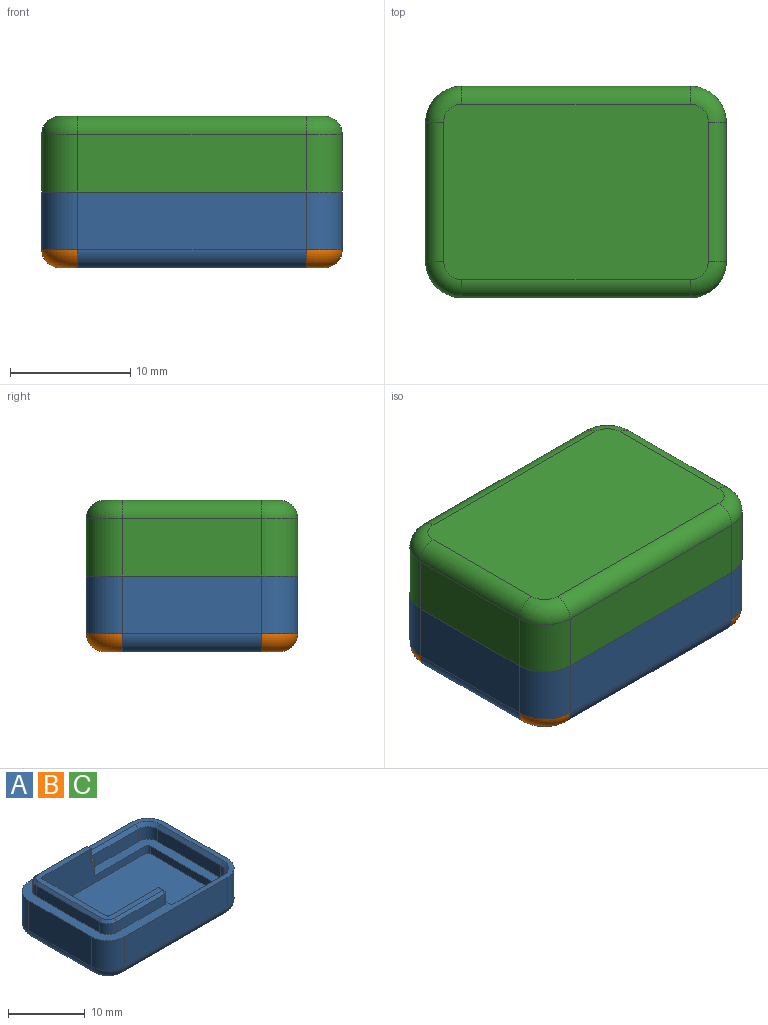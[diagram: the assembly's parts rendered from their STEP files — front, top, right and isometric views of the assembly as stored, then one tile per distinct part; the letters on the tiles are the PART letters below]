
ASSEMBLY  parts=3 mates=1
PART A: 61 faces, bbox 25.5x18.1x8.4 mm
  f0: plane 25x17.6mm, normal (0,0,1), area 80.8mm2, adj f3,f4,f6,f7,f8,f9,f10,f11
  f1: plane 11.6x1.2mm, normal (-1,0,0), area 13.9mm2, adj f2,f5,f18,f34
  f2: cylinder r=0.4mm len=1.2mm, axis (0,0,-1), area 0.8mm2, adj f1,f3,f18,f34
  f3: plane 19x5.8mm, normal (0,-1,0), area 65.1mm2, adj f0,f2,f15,f18,f28,f34,f35,f46
  f4: plane 19x5.8mm, normal (0,1,0), area 65.1mm2, adj f0,f5,f17,f18,f29,f34,f45,f46
  f5: cylinder r=0.4mm len=1.2mm, axis (0,0,-1), area 0.8mm2, adj f1,f4,f18,f34
  f6: plane 11.6x4.8mm, normal (1,0,0), area 55.7mm2, adj f0,f7,f13,f22
  f7: cylinder r=3mm len=4.8mm, axis (0,0,-1), area 22.6mm2, adj f0,f6,f8,f24
  f8: plane 19x4.8mm, normal (0,1,0), area 91.2mm2, adj f0,f7,f9,f26
  f9: cylinder r=3mm len=4.8mm, axis (0,0,-1), area 22.6mm2, adj f0,f8,f10,f25
  f10: plane 11.6x4.8mm, normal (-1,0,0), area 55.7mm2, adj f0,f9,f11,f23
  f11: cylinder r=3mm len=4.8mm, axis (0,0,-1), area 22.6mm2, adj f0,f10,f12,f21
  f12: plane 19x4.8mm, normal (0,-1,0), area 91.2mm2, adj f0,f11,f13,f19
  f13: cylinder r=3mm len=4.8mm, axis (0,0,-1), area 22.6mm2, adj f0,f6,f12,f20
  f14: plane 22x14.6mm, normal (0,0,-1), area 319.3mm2, adj f19,f20,f21,f22,f23,f24,f25,f26
  f15: cylinder r=0.4mm len=5.8mm, axis (0,0,-1), area 3.6mm2, adj f3,f16,f18,f46
  f16: plane 11.6x5.8mm, normal (1,0,0), area 67.3mm2, adj f15,f17,f18,f46
  f17: cylinder r=0.4mm len=5.8mm, axis (0,0,-1), area 3.6mm2, adj f4,f16,f18,f46
  f18: plane 19.8x12.4mm, normal (0,0,1), area 245.4mm2, adj f1,f2,f3,f4,f5,f15,f16,f17
  f19: cylinder r=1.5mm len=19mm, axis (1,0,0), area 44.8mm2, adj f12,f14,f20,f21
  f20: torus R=1.5mm, axis (0,0,1), area 9.1mm2, adj f13,f14,f19,f22
  f21: torus R=1.5mm, axis (0,0,1), area 9.1mm2, adj f11,f14,f19,f23
  f22: cylinder r=1.5mm len=11.6mm, axis (0,1,0), area 27.3mm2, adj f6,f14,f20,f24
  f23: cylinder r=1.5mm len=11.6mm, axis (0,-1,0), area 27.3mm2, adj f10,f14,f21,f25
  f24: torus R=1.5mm, axis (0,0,1), area 9.1mm2, adj f7,f14,f22,f26
  f25: torus R=1.5mm, axis (0,0,1), area 9.1mm2, adj f9,f14,f23,f26
  f26: cylinder r=1.5mm len=19mm, axis (-1,0,0), area 44.8mm2, adj f8,f14,f24,f25
  f27: plane 9.5x2mm, normal (0,-1,0), area 19mm2, adj f28,f33,f34,f47
  f28: plane 2.5x1.9mm, normal (1,0,0), area 3.6mm2, adj f0,f3,f27,f34,f47
  f29: plane 2.5x1.9mm, normal (1,0,0), area 3.6mm2, adj f0,f4,f30,f34,f51
  f30: plane 9.5x2mm, normal (0,1,0), area 19mm2, adj f29,f31,f34,f51
  f31: cylinder r=1.8mm len=2mm, axis (0,0,1), area 5.7mm2, adj f30,f32,f34,f50
  f32: plane 11.6x2mm, normal (-1,0,0), area 23.2mm2, adj f31,f33,f34,f49
  f33: cylinder r=1.8mm len=2mm, axis (0,0,1), area 5.7mm2, adj f27,f32,f34,f48
  f34: plane 15.2x11.3mm, normal (0,0,1), area 47.7mm2, adj f1,f2,f3,f4,f5,f27,f28,f29
  f35: cylinder r=0.5mm len=2.1mm, axis (0,0,-1), area 1.5mm2, adj f0,f3,f36,f46,f52
  f36: plane 1.7x0.2mm, normal (1,0,0), area 0.3mm2, adj f0,f35,f37,f52
  f37: cylinder r=0.5mm len=1.7mm, axis (0,0,-1), area 1.3mm2, adj f0,f36,f38,f53
  f38: plane 8.83x1.7mm, normal (0,1,0), area 15mm2, adj f0,f37,f39,f54
  f39: cylinder r=1.6mm len=1.7mm, axis (0,0,-1), area 4.3mm2, adj f0,f38,f40,f55
  f40: plane 11.6x1.7mm, normal (-1,0,0), area 19.7mm2, adj f0,f39,f41,f56
  f41: cylinder r=1.6mm len=1.7mm, axis (0,0,-1), area 4.3mm2, adj f0,f40,f42,f57
  f42: plane 8.83x1.7mm, normal (0,-1,0), area 15mm2, adj f0,f41,f43,f58
  f43: cylinder r=0.5mm len=1.7mm, axis (0,0,-1), area 1.3mm2, adj f0,f42,f44,f59
  f44: plane 1.7x0.2mm, normal (1,0,0), area 0.3mm2, adj f0,f43,f45,f60
  f45: cylinder r=0.5mm len=2.1mm, axis (0,0,-1), area 1.5mm2, adj f0,f4,f44,f46,f60
  f46: plane 14x10.13mm, normal (0,0,1), area 25.6mm2, adj f3,f4,f15,f16,f17,f35,f45,f52
  f47: plane 9.5x0.5mm, normal (0,-0.71,0.71), area 6.7mm2, adj f0,f27,f28,f48
  f48: cone r=1.8mm half-angle=45deg, axis (0,0,1), area 2.3mm2, adj f0,f33,f47,f49
  f49: plane 11.6x0.5mm, normal (-0.71,0,0.71), area 8.2mm2, adj f0,f32,f48,f50
  f50: cone r=1.8mm half-angle=45deg, axis (0,0,1), area 2.3mm2, adj f0,f31,f49,f51
  f51: plane 9.5x0.5mm, normal (0,0.71,0.71), area 6.7mm2, adj f0,f29,f30,f50
  f52: plane 0.69x0.4mm, normal (0.71,0,0.71), area 0.3mm2, adj f35,f36,f46,f53
  f53: cone r=0.5mm half-angle=45deg, axis (0,0,-1), area 0.3mm2, adj f37,f46,f52,f54
  f54: plane 8.83x0.4mm, normal (0,0.71,0.71), area 5mm2, adj f38,f46,f53,f55
  f55: cone r=1.2mm half-angle=45deg, axis (0,0,-1), area 1.2mm2, adj f39,f46,f54,f56
  f56: plane 11.6x0.4mm, normal (-0.71,0,0.71), area 6.6mm2, adj f40,f46,f55,f57
  f57: cone r=1.2mm half-angle=45deg, axis (0,0,-1), area 1.2mm2, adj f41,f46,f56,f58
  f58: plane 8.83x0.4mm, normal (0,-0.71,0.71), area 5mm2, adj f42,f46,f57,f59
  f59: cone r=0.1mm half-angle=45deg, axis (0,0,-1), area 0.3mm2, adj f43,f46,f58,f60
  f60: plane 0.69x0.4mm, normal (0.71,0,0.71), area 0.3mm2, adj f44,f45,f46,f59
PART B: same geometry as A
PART C: same geometry as A
PLACE A t=(-1.61,3.35,0.92)mm fixed
PLACE B t=(-1.61,3.35,0.92)mm
PLACE C rot(axis=(0,1,0),180deg) t=(-1.61,3.35,13.52)mm
MATE fastened C.f0 <-> A.f0  axis (0,0,-1) through (-14.11,-2.45,7.22)mm
